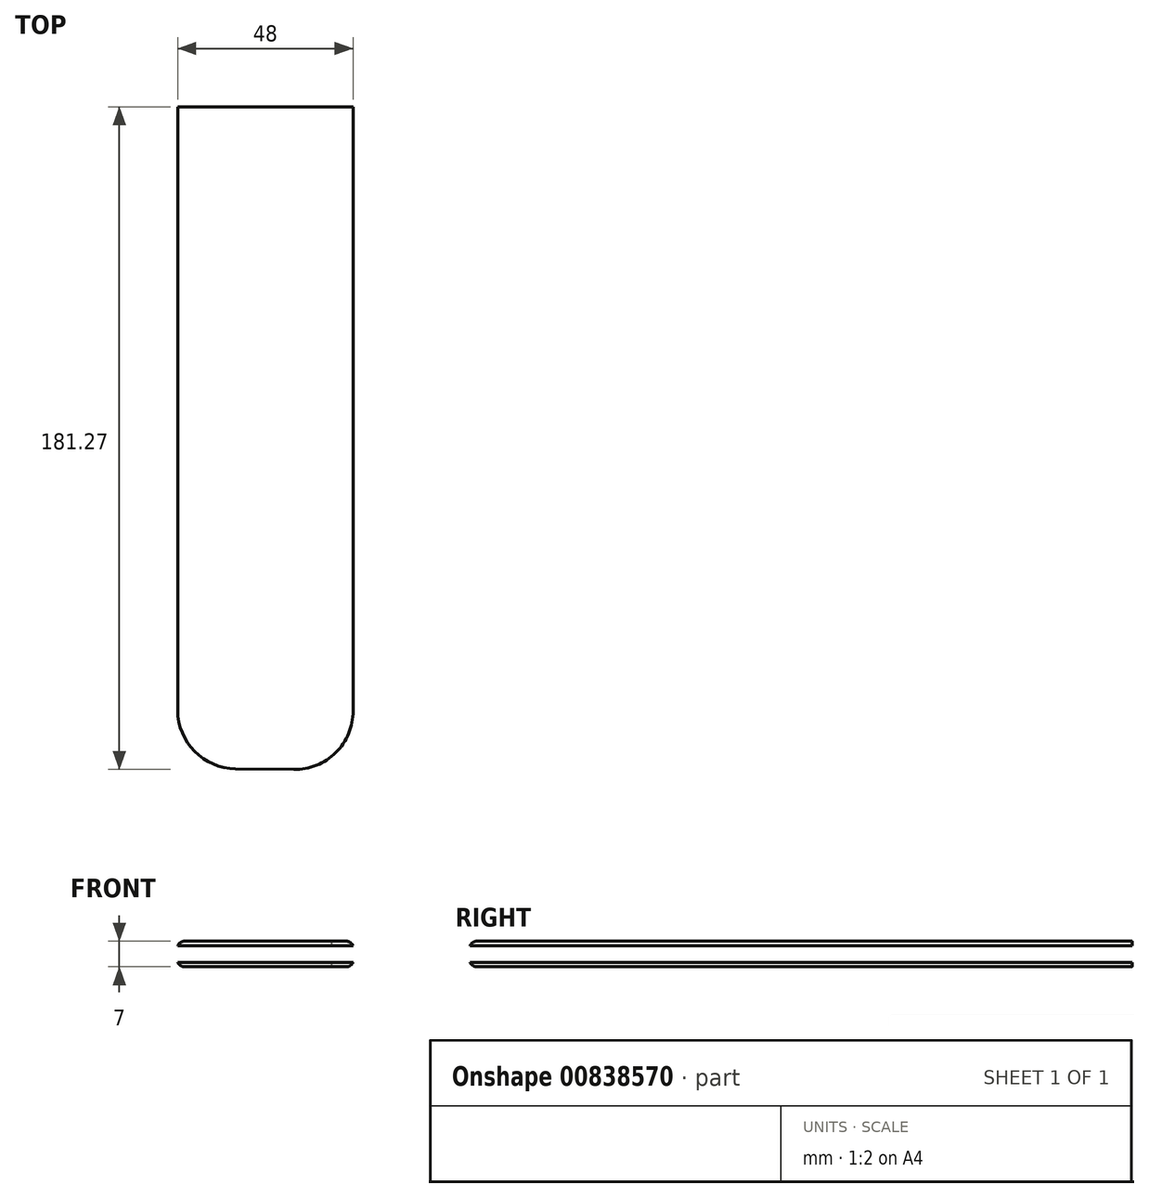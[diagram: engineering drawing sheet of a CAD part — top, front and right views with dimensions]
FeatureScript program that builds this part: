
annotation { "Feature Type Name" : "Feature", "Feature Type Description" : "" }
export const myFeature = defineFeature(function(context is Context, id is Id, definition is map)
    precondition{}
    {
        {
            var Q0;
            Q0=qCreatedBy(makeId("Top.planeOp"),FACE);
            var sketch = newSketch(context, id + "F0", { "sketchPlane" : qUnion([Q0])});
            skLineSegment(sketch, "E0", {"start": v(0, 61.3) * mm, "end": v(0, -148) * mm, "construction": true});
            skLineSegment(sketch, "E1", {"start": v(-18, 42.45) * mm, "end": v(18, 42.45) * mm});
            skLineSegment(sketch, "E2", {"start": v(-18, 42.45) * mm, "end": v(-18, -108) * mm});
            skLineSegment(sketch, "E3", {"start": v(18, -108.18) * mm, "end": v(18, 42.45) * mm});
            skPoint(sketch, "E4.visualSharp", {"position": v(-18, -132.43) * mm});
            skPoint(sketch, "E5.visualSharp", {"position": v(18, -132.87) * mm});
            skLineSegment(sketch, "E6.0", {"start": v(24, -122.75) * mm, "end": v(24, 42.52) * mm});
            skLineSegment(sketch, "E6.1", {"start": v(-24, 42.45) * mm, "end": v(-24, -122.55) * mm});
            skArc(sketch, "E6.2", {"start": v(-24, -122.55) * mm, "mid": v(-19.38, -133.8) * mm, "end": v(-8.2, -138.55) * mm});
            skLineSegment(sketch, "E6.3", {"start": v(-8.2, -138.55) * mm, "end": v(7.8, -138.75) * mm});
            skArc(sketch, "E6.4", {"start": v(7.8, -138.75) * mm, "mid": v(19.24, -134.13) * mm, "end": v(24, -122.75) * mm});
            skLineSegment(sketch, "E7", {"start": v(-18, 42.45) * mm, "end": v(-24, 42.45) * mm});
            skLineSegment(sketch, "E8", {"start": v(18, 42.45) * mm, "end": v(24, 42.52) * mm});
            skFitSpline(sketch, "E9", {"points": [v(-18, -108) * mm, v(-14.68, -122.87) * mm, v(-5.34, -131.89) * mm, v(0, -134.1) * mm], "startDerivative": vector(3.29, -40.09) * mm, "endDerivative": vector(20.34, -6.42) * mm});
            skSolve(sketch);
        }
        {
            var Q0;
            Q0=makeQuery(id+"F0.imprint","IMPRINT",FACE,{"disambiguationData":[TD([[makeQuery(id+"F0.imprint","IMPRINT",EDGE,{"derivedFrom":sQuery(id+"F0.wireOp",EDGE,"E2")}),-1.0]])]});
            var Q1;
            Q1=makeQuery(id+"F0.imprint","IMPRINT",FACE,{"disambiguationData":[TD([[makeQuery(id+"F0.imprint","IMPRINT",EDGE,{"derivedFrom":sQuery(id+"F0.wireOp",EDGE,"E1")}),-1.0]])]});
            extrude(context, id + "F1", {"entities" : qUnion([Q0, Q1]), "endBound" : BoundingType.SYMMETRIC, "depth" : 7 * mm, "offsetDistance" : 25 * mm});
        }
        {
            var Q0;
            Q0=makeQuery(id+"F0.imprint","IMPRINT",FACE,{"disambiguationData":[TD([[makeQuery(id+"F0.imprint","IMPRINT",EDGE,{"derivedFrom":sQuery(id+"F0.wireOp",EDGE,"E1")}),-1.0]])]});
            extrude(context, id + "F2", {"entities" : qUnion([Q0]), "operationType" : NewBodyOperationType.REMOVE, "endBound" : BoundingType.SYMMETRIC, "oppositeDirection" : true, "depth" : 4.5 * mm, "offsetDistance" : 25 * mm});
        }
        {
            var Q0;
            Q0=makeQuery(id+"F1.opExtrude","CAP_EDGE",EDGE,{"disambiguationData":[OSD([sQuery(id+"F0.wireOp",EDGE,"E6.0")])],"isStart":false});
            var Q1;
            Q1=makeQuery(id+"F1.opExtrude","CAP_EDGE",EDGE,{"disambiguationData":[OSD([sQuery(id+"F0.wireOp",EDGE,"E6.0")])],"isStart":true});
            fillet(context, id + "F3", {"entities" : qUnion([Q0, Q1]), "radius" : 2 * mm, "tangentPropagation" : true, "allowEdgeOverflow" : false});
        }
    });
